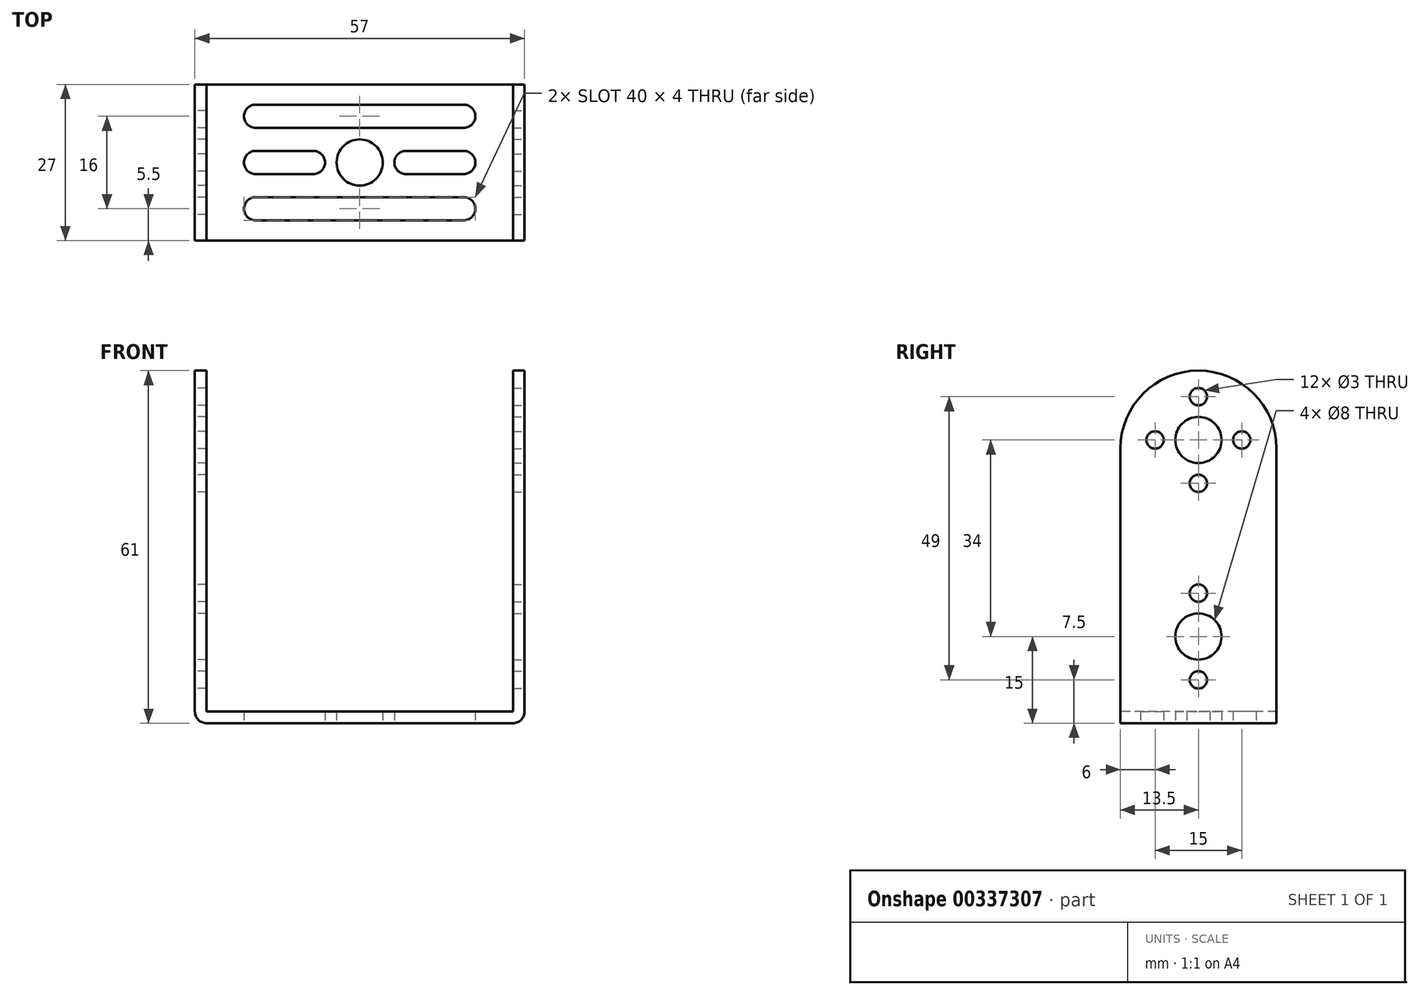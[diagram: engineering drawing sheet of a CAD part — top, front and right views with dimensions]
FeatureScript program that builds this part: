
annotation { "Feature Type Name" : "Feature", "Feature Type Description" : "" }
export const myFeature = defineFeature(function(context is Context, id is Id, definition is map)
    precondition{}
    {
        {
            var Q0;
            Q0=qCreatedBy(makeId("Top.planeOp"),FACE);
            var sketch = newSketch(context, id + "F0", { "sketchPlane" : qUnion([Q0])});
            skLineSegment(sketch, "E0.bottom", {"start": v(28.5, 13.5) * mm, "end": v(-28.5, 13.5) * mm});
            skLineSegment(sketch, "E0.top", {"start": v(28.5, -13.5) * mm, "end": v(-28.5, -13.5) * mm});
            skLineSegment(sketch, "E0.left", {"start": v(28.5, 13.5) * mm, "end": v(28.5, -13.5) * mm});
            skLineSegment(sketch, "E0.right", {"start": v(-28.5, 13.5) * mm, "end": v(-28.5, -13.5) * mm});
            skPoint(sketch, "E0.middle", {"position": v(0, 0) * mm});
            skCircle(sketch, "E1", {"center": v(0, 0) * mm, "radius": 4 * mm});
            skLineSegment(sketch, "E2.bottom", {"start": v(-18, 10) * mm, "end": v(18, 10) * mm});
            skLineSegment(sketch, "E2.top", {"start": v(-18, 6) * mm, "end": v(18, 6) * mm});
            skLineSegment(sketch, "E2.left", {"start": v(-18, 10) * mm, "end": v(-18, 6) * mm});
            skLineSegment(sketch, "E2.right", {"start": v(18, 10) * mm, "end": v(18, 6) * mm});
            skLineSegment(sketch, "E3.bottom", {"start": v(-18, 2) * mm, "end": v(-8, 2) * mm});
            skLineSegment(sketch, "E3.top", {"start": v(-18, -2) * mm, "end": v(-8, -2) * mm});
            skLineSegment(sketch, "E3.left", {"start": v(-18, 2) * mm, "end": v(-18, -2) * mm});
            skLineSegment(sketch, "E3.right", {"start": v(-8, 2) * mm, "end": v(-8, -2) * mm});
            skLineSegment(sketch, "E4.bottom", {"start": v(8, 2) * mm, "end": v(18, 2) * mm});
            skLineSegment(sketch, "E4.top", {"start": v(8, -2) * mm, "end": v(18, -2) * mm});
            skLineSegment(sketch, "E4.left", {"start": v(8, 2) * mm, "end": v(8, -2) * mm});
            skLineSegment(sketch, "E4.right", {"start": v(18, 2) * mm, "end": v(18, -2) * mm});
            skLineSegment(sketch, "E5.bottom", {"start": v(-18, -6) * mm, "end": v(18, -6) * mm});
            skLineSegment(sketch, "E5.top", {"start": v(-18, -10) * mm, "end": v(18, -10) * mm});
            skLineSegment(sketch, "E5.left", {"start": v(-18, -6) * mm, "end": v(-18, -10) * mm});
            skLineSegment(sketch, "E5.right", {"start": v(18, -6) * mm, "end": v(18, -10) * mm});
            skArc(sketch, "E6", {"start": v(-18, 2) * mm, "mid": v(-20, 0) * mm, "end": v(-18, -2) * mm});
            skArc(sketch, "E7", {"start": v(-8, -2) * mm, "mid": v(-6, 0) * mm, "end": v(-8, 2) * mm});
            skArc(sketch, "E8", {"start": v(-18, 10) * mm, "mid": v(-20, 8) * mm, "end": v(-18, 6) * mm});
            skArc(sketch, "E9", {"start": v(18, 6) * mm, "mid": v(20, 8) * mm, "end": v(18, 10) * mm});
            skArc(sketch, "E10", {"start": v(8, 2) * mm, "mid": v(6, 0) * mm, "end": v(8, -2) * mm});
            skArc(sketch, "E11", {"start": v(18, -2) * mm, "mid": v(20, 0) * mm, "end": v(18, 2) * mm});
            skArc(sketch, "E12", {"start": v(18, -10) * mm, "mid": v(20, -8) * mm, "end": v(18, -6) * mm});
            skArc(sketch, "E13", {"start": v(-18, -6) * mm, "mid": v(-20, -8) * mm, "end": v(-18, -10) * mm});
            skPoint(sketch, "E14", {"position": v(0, 6) * mm});
            skPoint(sketch, "E15", {"position": v(0, -6) * mm});
            skSolve(sketch);
        }
        {
            var Q0;
            Q0=sQuery(id+"F0.wireOp",EDGE,"E0.left");
            var Q1;
            Q1=qCreatedBy(makeId("Right.planeOp"),FACE);
            cPlane(context, id + "F1", {"entities" : qUnion([Q0, Q1]), "cplaneType" : CPlaneType.LINE_ANGLE, "offset" : 25.4 * mm, "angle" : 0 * degree, "width" : 152.4 * mm, "height" : 152.4 * mm});
        }
        {
            var Q0;
            Q0=sQuery(id+"F0.wireOp",EDGE,"E0.right");
            var Q1;
            Q1=qCreatedBy(makeId("Right.planeOp"),FACE);
            cPlane(context, id + "F2", {"entities" : qUnion([Q0, Q1]), "cplaneType" : CPlaneType.LINE_ANGLE, "offset" : 25.4 * mm, "angle" : 0 * degree, "width" : 152.4 * mm, "height" : 152.4 * mm});
        }
        {
            var Q0;
            Q0=qCreatedBy(id+"F1.planeOp",FACE);
            var sketch = newSketch(context, id + "F3", { "sketchPlane" : qUnion([Q0])});
            skLineSegment(sketch, "E16.bottom", {"start": v(13.5, 0) * mm, "end": v(-13.5, 0) * mm});
            skLineSegment(sketch, "E16.top", {"start": v(13.5, 47.5) * mm, "end": v(-13.5, 47.5) * mm});
            skLineSegment(sketch, "E16.left", {"start": v(13.5, 0) * mm, "end": v(13.5, 47.5) * mm});
            skLineSegment(sketch, "E16.right", {"start": v(-13.5, 0) * mm, "end": v(-13.5, 47.5) * mm});
            skArc(sketch, "E17", {"start": v(13.5, 47.5) * mm, "mid": v(0, 61) * mm, "end": v(-13.5, 47.5) * mm});
            skCircle(sketch, "E18", {"center": v(0, 15) * mm, "radius": 4 * mm});
            skCircle(sketch, "E19", {"center": v(0, 7.5) * mm, "radius": 1.5 * mm});
            skCircle(sketch, "E20", {"center": v(0, 22.5) * mm, "radius": 1.5 * mm});
            skCircle(sketch, "E21", {"center": v(0, 49) * mm, "radius": 4 * mm});
            skCircle(sketch, "E22", {"center": v(-7.5, 49) * mm, "radius": 1.5 * mm});
            skCircle(sketch, "E23", {"center": v(0, 56.5) * mm, "radius": 1.5 * mm});
            skCircle(sketch, "E24", {"center": v(0, 41.5) * mm, "radius": 1.5 * mm});
            skCircle(sketch, "E25", {"center": v(7.5, 49) * mm, "radius": 1.5 * mm});
            skSolve(sketch);
        }
        {
            var Q0;
            Q0=qCreatedBy(id+"F2.planeOp",FACE);
            var sketch = newSketch(context, id + "F4", { "sketchPlane" : qUnion([Q0])});
            skLineSegment(sketch, "E26.bottom", {"start": v(13.5, 0) * mm, "end": v(-13.5, 0) * mm});
            skLineSegment(sketch, "E26.top", {"start": v(13.5, 47.5) * mm, "end": v(-13.5, 47.5) * mm});
            skLineSegment(sketch, "E26.left", {"start": v(13.5, 0) * mm, "end": v(13.5, 47.5) * mm});
            skLineSegment(sketch, "E26.right", {"start": v(-13.5, 0) * mm, "end": v(-13.5, 47.5) * mm});
            skArc(sketch, "E27", {"start": v(13.5, 47.5) * mm, "mid": v(0, 61) * mm, "end": v(-13.5, 47.5) * mm});
            skCircle(sketch, "E28", {"center": v(0, 15) * mm, "radius": 4 * mm});
            skCircle(sketch, "E29", {"center": v(0, 7.5) * mm, "radius": 1.5 * mm});
            skCircle(sketch, "E30", {"center": v(0, 22.5) * mm, "radius": 1.5 * mm});
            skCircle(sketch, "E31", {"center": v(0, 49) * mm, "radius": 4 * mm});
            skCircle(sketch, "E32", {"center": v(-7.5, 49) * mm, "radius": 1.5 * mm});
            skCircle(sketch, "E33", {"center": v(0, 56.5) * mm, "radius": 1.5 * mm});
            skCircle(sketch, "E34", {"center": v(0, 41.5) * mm, "radius": 1.5 * mm});
            skCircle(sketch, "E35", {"center": v(7.5, 49) * mm, "radius": 1.5 * mm});
            skSolve(sketch);
        }
        {
            var Q0;
            Q0=makeQuery(id+"F0.imprint","IMPRINT",FACE,{"disambiguationData":[TD([[makeQuery(id+"F0.imprint","IMPRINT",EDGE,{"derivedFrom":sQuery(id+"F0.wireOp",EDGE,"E0.bottom")}),1.0]])]});
            extrude(context, id + "F5", {"entities" : qUnion([Q0]), "depth" : 2 * mm});
        }
        {
            var Q0;
            Q0=makeQuery(id+"F4.imprint","IMPRINT",FACE,{"disambiguationData":[TD([[makeQuery(id+"F4.imprint","IMPRINT",EDGE,{"derivedFrom":sQuery(id+"F4.wireOp",EDGE,"E26.bottom")}),-1.0]])]});
            var Q1;
            {var subQ0=sQuery(id+"F4.wireOp",EDGE,"E27");Q1=makeQuery(id+"F4.imprint","IMPRINT",FACE,{"disambiguationData":[TD([[makeQuery(id+"F4.imprint","IMPRINT",EDGE,{"derivedFrom":subQ0}),1.0]])]});}
            extrude(context, id + "F6", {"entities" : qUnion([Q0, Q1]), "operationType" : NewBodyOperationType.ADD, "oppositeDirection" : true, "depth" : 2 * mm});
        }
        {
            var Q0;
            Q0=makeQuery(id+"F3.imprint","IMPRINT",FACE,{"disambiguationData":[TD([[makeQuery(id+"F3.imprint","IMPRINT",EDGE,{"derivedFrom":sQuery(id+"F3.wireOp",EDGE,"E16.bottom")}),-1.0]])]});
            var Q1;
            {var subQ0=sQuery(id+"F3.wireOp",EDGE,"E17");Q1=makeQuery(id+"F3.imprint","IMPRINT",FACE,{"disambiguationData":[TD([[makeQuery(id+"F3.imprint","IMPRINT",EDGE,{"derivedFrom":subQ0}),1.0]])]});}
            extrude(context, id + "F7", {"entities" : qUnion([Q0, Q1]), "operationType" : NewBodyOperationType.ADD, "depth" : 2 * mm});
        }
        {
            var Q0;
            Q0=makeQuery(id+"F5.opExtrude","CAP_EDGE",EDGE,{"disambiguationData":[OSD([sQuery(id+"F0.wireOp",EDGE,"E0.right")])],"isStart":true});
            var Q1;
            Q1=makeQuery(id+"F5.opExtrude","CAP_EDGE",EDGE,{"disambiguationData":[OSD([sQuery(id+"F0.wireOp",EDGE,"E0.left")])],"isStart":true});
            fillet(context, id + "F8", {"entities" : qUnion([Q0, Q1]), "radius" : 2 * mm, "tangentPropagation" : true, "allowEdgeOverflow" : false});
        }
    });
